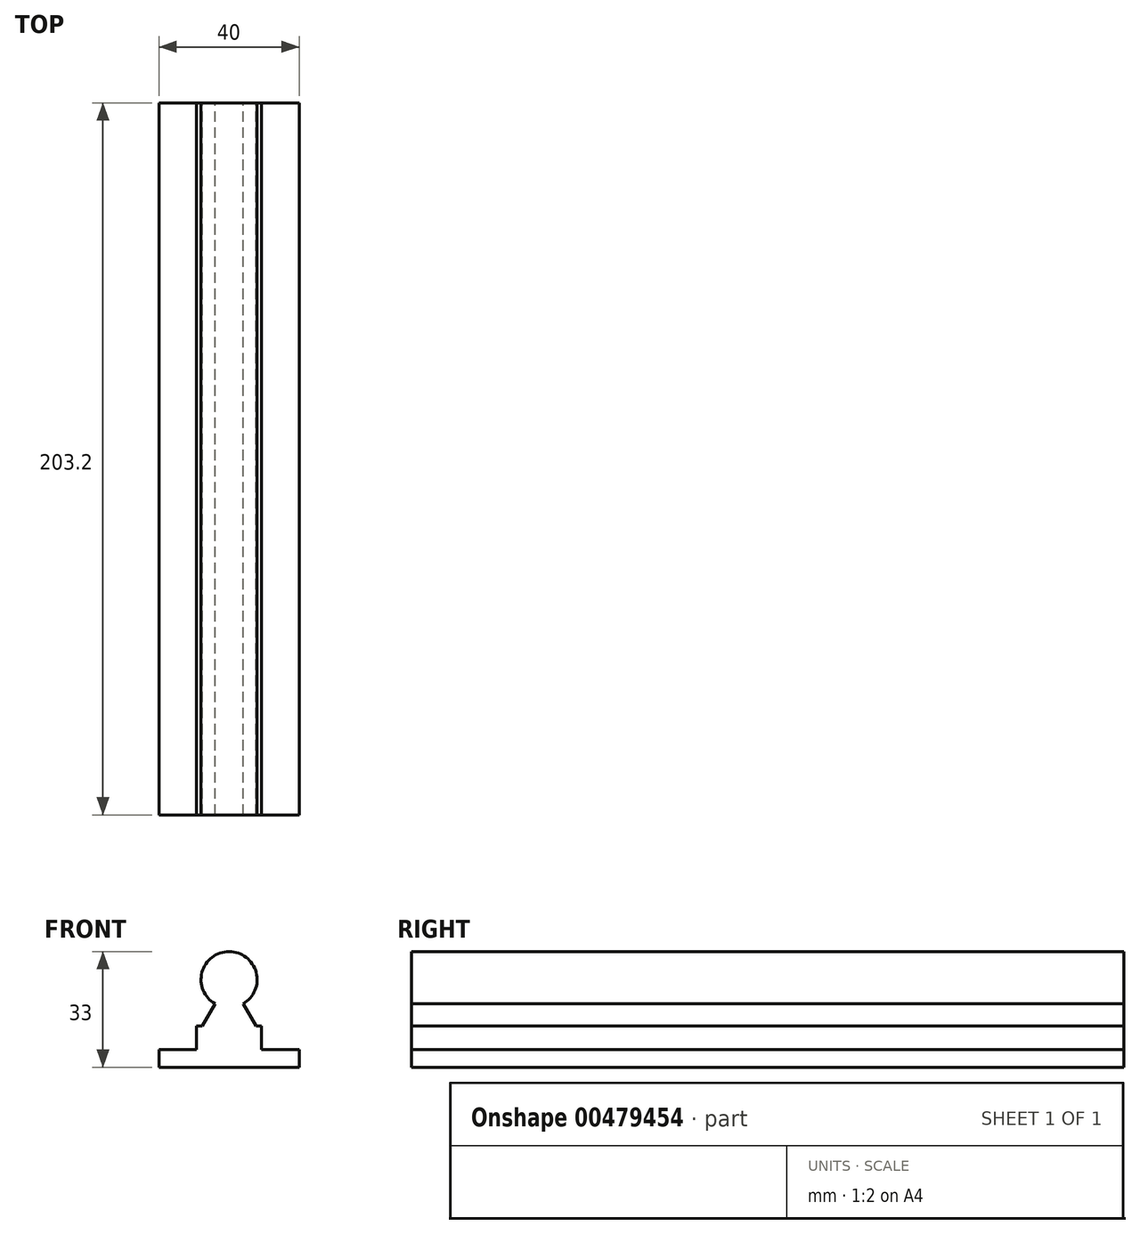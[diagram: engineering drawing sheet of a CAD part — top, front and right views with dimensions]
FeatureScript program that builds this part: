
annotation { "Feature Type Name" : "Feature", "Feature Type Description" : "" }
export const myFeature = defineFeature(function(context is Context, id is Id, definition is map)
    precondition{}
    {
        {
            var Q0;
            Q0=qCreatedBy(makeId("Front.planeOp"),FACE);
            var sketch = newSketch(context, id + "F0", { "sketchPlane" : qUnion([Q0])});
            skCircle(sketch, "E0", {"center": v(0, 0) * mm, "radius": 8 * mm});
            skLineSegment(sketch, "E1", {"start": v(-4, -6.93) * mm, "end": v(-7.68, -13.3) * mm});
            skLineSegment(sketch, "E2", {"start": v(-7.68, -13.3) * mm, "end": v(-9.25, -13.3) * mm});
            skLineSegment(sketch, "E3", {"start": v(-9.25, -13.3) * mm, "end": v(-9.25, -20) * mm});
            skLineSegment(sketch, "E4", {"start": v(-9.25, -20) * mm, "end": v(-20, -20) * mm});
            skLineSegment(sketch, "E5", {"start": v(-20, -20) * mm, "end": v(-20, -25) * mm});
            skLineSegment(sketch, "E6", {"start": v(-20, -25) * mm, "end": v(0, -25) * mm});
            skLineSegment(sketch, "E7.MirrorCS", {"start": v(20, -25) * mm, "end": v(0, -25) * mm});
            skLineSegment(sketch, "E8.MirrorCS", {"start": v(20, -20) * mm, "end": v(20, -25) * mm});
            skLineSegment(sketch, "E9.MirrorCS", {"start": v(9.25, -20) * mm, "end": v(20, -20) * mm});
            skLineSegment(sketch, "E10.MirrorCS", {"start": v(9.25, -13.3) * mm, "end": v(9.25, -20) * mm});
            skLineSegment(sketch, "E11.MirrorCS", {"start": v(4, -6.93) * mm, "end": v(7.68, -13.3) * mm});
            skLineSegment(sketch, "E12.MirrorCS", {"start": v(7.68, -13.3) * mm, "end": v(9.25, -13.3) * mm});
            skSolve(sketch);
        }
        {
            var Q0;
            Q0=qSketchRegion(id+"F0",true);
            extrude(context, id + "F1", {"entities" : qUnion([Q0]), "depth" : 203.2 * mm});
        }
    });
